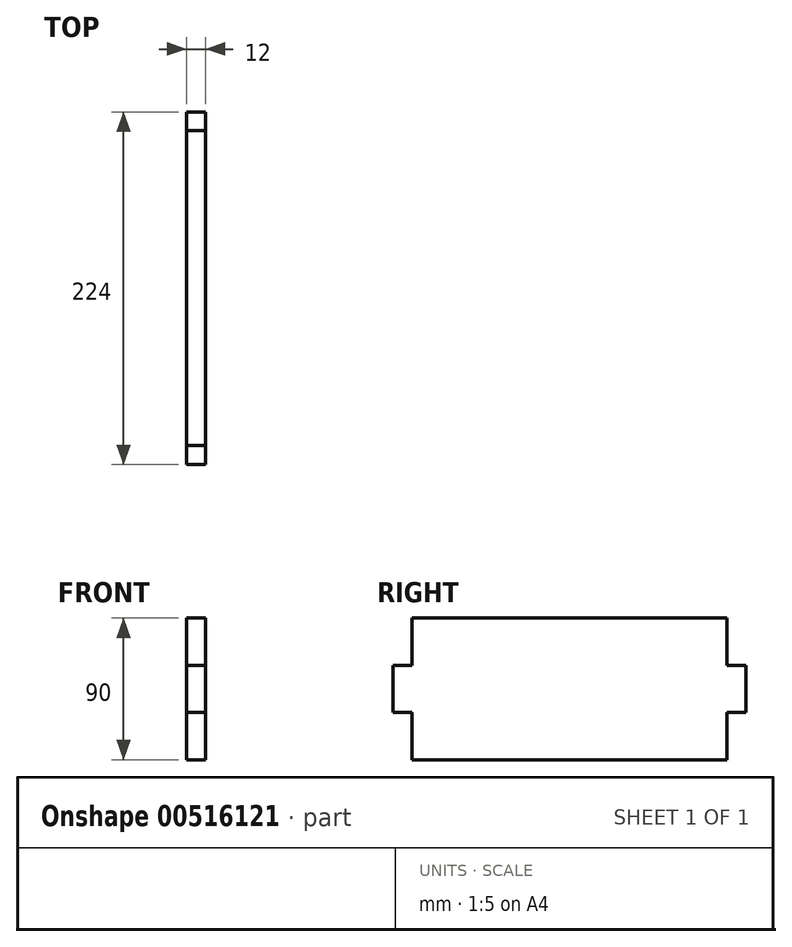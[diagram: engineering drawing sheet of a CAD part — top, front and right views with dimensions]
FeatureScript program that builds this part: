
annotation { "Feature Type Name" : "Feature", "Feature Type Description" : "" }
export const myFeature = defineFeature(function(context is Context, id is Id, definition is map)
    precondition{}
    {
        {
            var Q0;
            Q0=qCreatedBy(makeId("Right.planeOp"),FACE);
            var sketch = newSketch(context, id + "F0", { "sketchPlane" : qUnion([Q0])});
            skLineSegment(sketch, "E0", {"start": v(0, 0) * mm, "end": v(0, 30) * mm});
            skLineSegment(sketch, "E1", {"start": v(0, 30) * mm, "end": v(-12, 30) * mm});
            skLineSegment(sketch, "E2", {"start": v(-12, 30) * mm, "end": v(-12, 60) * mm});
            skLineSegment(sketch, "E3", {"start": v(-12, 60) * mm, "end": v(0, 60) * mm});
            skLineSegment(sketch, "E4", {"start": v(0, 60) * mm, "end": v(0, 90) * mm});
            skLineSegment(sketch, "E5", {"start": v(0, 90) * mm, "end": v(100, 90) * mm});
            skLineSegment(sketch, "E6", {"start": v(100, 90) * mm, "end": v(100, 0) * mm, "construction": true});
            skLineSegment(sketch, "E7", {"start": v(100, 0) * mm, "end": v(0, 0) * mm});
            skLineSegment(sketch, "E8.MirrorCS", {"start": v(200, 90) * mm, "end": v(100, 90) * mm});
            skLineSegment(sketch, "E9.MirrorCS", {"start": v(100, 0) * mm, "end": v(200, 0) * mm});
            skLineSegment(sketch, "E10.MirrorCS", {"start": v(200, 60) * mm, "end": v(200, 90) * mm});
            skLineSegment(sketch, "E11.MirrorCS", {"start": v(212, 30) * mm, "end": v(212, 60) * mm});
            skLineSegment(sketch, "E12.MirrorCS", {"start": v(200, 30) * mm, "end": v(212, 30) * mm});
            skLineSegment(sketch, "E13.MirrorCS", {"start": v(200, 0) * mm, "end": v(200, 30) * mm});
            skLineSegment(sketch, "E14.MirrorCS", {"start": v(212, 60) * mm, "end": v(200, 60) * mm});
            skSolve(sketch);
        }
        {
            var Q0;
            Q0 = qSketchRegion(id + "F0", true);
            extrude(context, id + "F1", {"entities" : qUnion([Q0]), "endBound" : BoundingType.SYMMETRIC, "depth" : 12 * mm, "offsetDistance" : 25 * mm});
        }
    });
